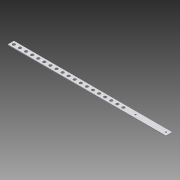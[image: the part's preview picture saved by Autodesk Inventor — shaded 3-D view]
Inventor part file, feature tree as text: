
AUTODESK INVENTOR PART (.ipt)
format: ipt  version: 2015 (Build 190159000, 159)  size: 129,024 bytes
history: native  units: in
note: dims shown in document units (in); Inventor stores cm internally (conversion verified against a paired STEP export)
features: sketch x5, other x3
ambient origin geometry x8: Origin, YZ Plane, XZ Plane, XY Plane, X Axis, Y Axis, Z Axis, Center Point
bodies: Solid1 (feature_tree)
feature tree (8):
  other  "bottom clamper arm.ipt"
  other  "Solid1::bottom clamper arm.ipt"
  other  "TaggingFeature1"
  sketch  "Sketch1"  dims[d0=0.3937in]
  sketch  "Sketch2"
  sketch  "Sketch3"
  sketch  "Sketch4"
  sketch  "Sketch5"
